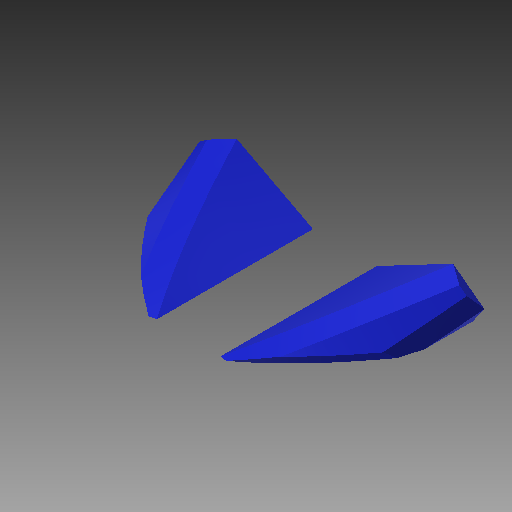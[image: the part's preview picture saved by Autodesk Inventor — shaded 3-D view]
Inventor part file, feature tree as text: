
AUTODESK INVENTOR PART (.ipt)
format: ipt  version: 2017.2 (Build 212233000, 233)  size: 227,328 bytes
history: native  units: in
note: dims shown in document units (in); Inventor stores cm internally (conversion verified against a paired STEP export)
features: sketch x3, plane x1, loft x1, extrude x1, chamfer x1
ambient origin geometry x8: Origin, YZ Plane, XZ Plane, XY Plane, X Axis, Y Axis, Z Axis, Center Point
bodies: Solid1 (feature_tree)
feature tree (7):
  sketch  "Sketch1"  dims[d0=0.7559in d1=0.7559in]
  plane  "Work Plane1"
  loft  "Main Body"
  extrude  "Create Eyes"  Depth=0.2in
  chamfer  "Eyes Chamfer"  Distance=0.08in
  sketch  "Sketch2"  dims[d2=0.9963in d3=0.2in]
  sketch  "Sketch3"  dims[d4=0.5in d6=0.08in d7=0.55in d8=150.0deg d9=150.0deg d14=0.33in d15=0.66in d18=0.0in d19=90.0deg d20=0.0in d21=90.0deg d22=1.0in d26=1.0651in d28=1.0651in d29=0.0in d30=0.962in d31=0.962in d32=0.075in d33=0.15in d34=0.06in d35=0.1in d36=0.05in d37=0.45in d38=0.0in d125=0.02in d126=0.125in d127=45.0deg]
